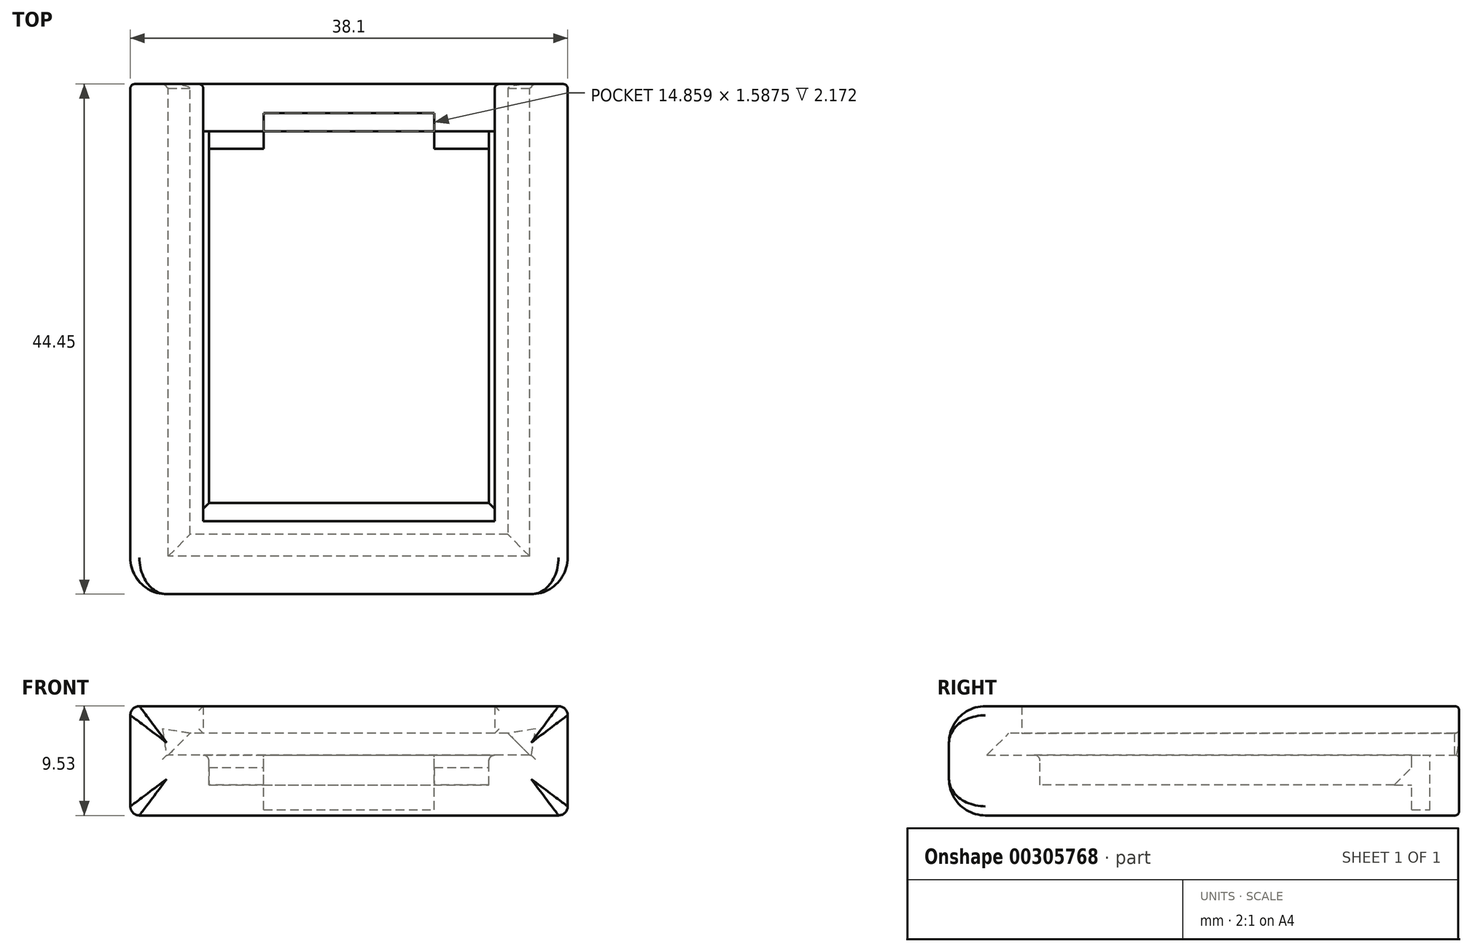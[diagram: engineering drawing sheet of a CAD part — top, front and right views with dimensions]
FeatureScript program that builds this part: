
annotation { "Feature Type Name" : "Feature", "Feature Type Description" : "" }
export const myFeature = defineFeature(function(context is Context, id is Id, definition is map)
    precondition{}
    {
        {
            var Q0;
            Q0=qCreatedBy(makeId("Top.planeOp"),FACE);
            var sketch = newSketch(context, id + "F0", { "sketchPlane" : qUnion([Q0])});
            skLineSegment(sketch, "E0.bottom", {"start": v(0, 0) * mm, "end": v(38.1, 0) * mm});
            skLineSegment(sketch, "E0.top", {"start": v(0, 44.45) * mm, "end": v(38.1, 44.45) * mm});
            skLineSegment(sketch, "E0.left", {"start": v(0, 0) * mm, "end": v(0, 44.45) * mm});
            skLineSegment(sketch, "E0.right", {"start": v(38.1, 0) * mm, "end": v(38.1, 44.45) * mm});
            skSolve(sketch);
        }
        {
            var Q0;
            Q0=makeQuery(id+"F0.imprint","IMPRINT",FACE,{"disambiguationData":[TD([[makeQuery(id+"F0.imprint","IMPRINT",EDGE,{"derivedFrom":sQuery(id+"F0.wireOp",EDGE,"E0.bottom")}),1.0]])]});
            extrude(context, id + "F1", {"entities" : qUnion([Q0]), "depth" : 9.52 * mm});
        }
        {
            var Q0;
            Q0=makeQuery(id+"F1.opExtrude","CAP_FACE",FACE,{"disambiguationData":[OSD([sQuery(id+"F0.wireOp",EDGE,"E0.bottom"),sQuery(id+"F0.wireOp",EDGE,"E0.top"),sQuery(id+"F0.wireOp",EDGE,"E0.left"),sQuery(id+"F0.wireOp",EDGE,"E0.right")])],"isStart":false});
            var sketch = newSketch(context, id + "F2", { "sketchPlane" : qUnion([Q0])});
            skLineSegment(sketch, "E1.bottom", {"start": v(6.86, 40.32) * mm, "end": v(31.24, 40.32) * mm});
            skLineSegment(sketch, "E1.top", {"start": v(6.86, 7.94) * mm, "end": v(31.24, 7.94) * mm});
            skLineSegment(sketch, "E1.left", {"start": v(6.86, 40.32) * mm, "end": v(6.86, 7.94) * mm});
            skLineSegment(sketch, "E1.right", {"start": v(31.24, 40.32) * mm, "end": v(31.24, 7.94) * mm});
            skSolve(sketch);
        }
        {
            var Q0;
            Q0=makeQuery(id+"F2.imprint","IMPRINT",FACE,{"disambiguationData":[TD([[makeQuery(id+"F2.imprint","IMPRINT",EDGE,{"derivedFrom":sQuery(id+"F2.wireOp",EDGE,"E1.bottom")}),-1.0]])]});
            extrude(context, id + "F3", {"entities" : qUnion([Q0]), "operationType" : NewBodyOperationType.REMOVE, "oppositeDirection" : true, "depth" : 6.86 * mm});
        }
        {
            var Q0;
            Q0=makeQuery(id+"F1.opExtrude","SWEPT_FACE",FACE,{"disambiguationData":[OSD([sQuery(id+"F0.wireOp",EDGE,"E0.top")])]});
            var sketch = newSketch(context, id + "F4", { "sketchPlane" : qUnion([Q0])});
            skLineSegment(sketch, "E2.bottom", {"start": v(-34.92, 7.16) * mm, "end": v(-3.17, 7.16) * mm});
            skLineSegment(sketch, "E2.top", {"start": v(-34.92, 5.26) * mm, "end": v(-3.17, 5.26) * mm});
            skLineSegment(sketch, "E2.left", {"start": v(-34.92, 7.16) * mm, "end": v(-34.92, 5.26) * mm});
            skLineSegment(sketch, "E2.right", {"start": v(-3.17, 7.16) * mm, "end": v(-3.17, 5.26) * mm});
            skSolve(sketch);
        }
        {
            var Q0;
            Q0=makeQuery(id+"F4.imprint","IMPRINT",FACE,{"disambiguationData":[TD([[makeQuery(id+"F4.imprint","IMPRINT",EDGE,{"derivedFrom":sQuery(id+"F4.wireOp",EDGE,"E2.bottom")}),-1.0]])]});
            extrude(context, id + "F5", {"entities" : qUnion([Q0]), "operationType" : NewBodyOperationType.REMOVE, "oppositeDirection" : true, "depth" : 41.27 * mm});
        }
        {
            var Q0;
            Q0=makeQuery(id+"F1.opExtrude","SWEPT_FACE",FACE,{"disambiguationData":[OSD([sQuery(id+"F0.wireOp",EDGE,"E0.top")])]});
            var sketch = newSketch(context, id + "F6", { "sketchPlane" : qUnion([Q0])});
            skLineSegment(sketch, "E3.bottom", {"start": v(-31.75, 9.53) * mm, "end": v(-6.35, 9.53) * mm});
            skLineSegment(sketch, "E3.top", {"start": v(-31.75, 7.16) * mm, "end": v(-6.35, 7.16) * mm});
            skLineSegment(sketch, "E3.left", {"start": v(-31.75, 9.53) * mm, "end": v(-31.75, 7.16) * mm});
            skLineSegment(sketch, "E3.right", {"start": v(-6.35, 9.53) * mm, "end": v(-6.35, 7.16) * mm});
            skSolve(sketch);
        }
        {
            var Q0;
            Q0=makeQuery(id+"F6.imprint","IMPRINT",FACE,{"disambiguationData":[TD([[makeQuery(id+"F6.imprint","IMPRINT",EDGE,{"derivedFrom":sQuery(id+"F6.wireOp",EDGE,"E3.bottom")}),1.0]])]});
            extrude(context, id + "F7", {"entities" : qUnion([Q0]), "operationType" : NewBodyOperationType.REMOVE, "oppositeDirection" : true, "depth" : 38.1 * mm});
        }
        {
            var Q0;
            Q0=makeQuery(id+"F5.boolean.opBoolean","COPY",FACE,{"derivedFrom":makeQuery(id+"F5.opExtrude","SWEPT_FACE",FACE,{"disambiguationData":[OSD([sQuery(id+"F4.wireOp",EDGE,"E2.top")])]})});
            var sketch = newSketch(context, id + "F8", { "sketchPlane" : qUnion([Q0])});
            skLineSegment(sketch, "E4.bottom", {"start": v(11.62, 40.32) * mm, "end": v(26.48, 40.32) * mm});
            skLineSegment(sketch, "E4.top", {"start": v(11.62, 41.91) * mm, "end": v(26.48, 41.91) * mm});
            skLineSegment(sketch, "E4.left", {"start": v(11.62, 40.32) * mm, "end": v(11.62, 41.91) * mm});
            skLineSegment(sketch, "E4.right", {"start": v(26.48, 40.32) * mm, "end": v(26.48, 41.91) * mm});
            skSolve(sketch);
        }
        {
            var Q0;
            Q0=makeQuery(id+"F8.imprint","IMPRINT",FACE,{"disambiguationData":[TD([[makeQuery(id+"F8.imprint","IMPRINT",EDGE,{"derivedFrom":sQuery(id+"F8.wireOp",EDGE,"E4.bottom")}),1.0]])]});
            extrude(context, id + "F9", {"entities" : qUnion([Q0]), "operationType" : NewBodyOperationType.REMOVE, "oppositeDirection" : true, "depth" : 4.76 * mm});
        }
        {
            var Q0;
            {var subQ0=sQuery(id+"F2.wireOp",EDGE,"E1.bottom");Q0=makeQuery(id+"F9.boolean.opBoolean","SPLIT",EDGE,{"disambiguationData":[topologyDisambiguationEdgeConnected([makeQuery(id+"F3.boolean.opBoolean","COPY",FACE,{"derivedFrom":makeQuery(id+"F3.opExtrude","CAP_FACE",FACE,{"disambiguationData":[OSD([subQ0,sQuery(id+"F2.wireOp",EDGE,"E1.top"),sQuery(id+"F2.wireOp",EDGE,"E1.left"),sQuery(id+"F2.wireOp",EDGE,"E1.right")])],"isStart":false})}),makeQuery(id+"F9.opExtrude","SWEPT_FACE",FACE,{"disambiguationData":[OSD([sQuery(id+"F8.wireOp",EDGE,"E4.bottom")])]})])],"derivedFrom":makeQuery(id+"F3.boolean.opBoolean","COPY",EDGE,{"derivedFrom":makeQuery(id+"F3.opExtrude","CAP_EDGE",EDGE,{"disambiguationData":[OSD([subQ0])],"isStart":false})})});}
            var Q1;
            Q1=makeQuery(id+"F9.boolean.opBoolean","COPY",EDGE,{"derivedFrom":makeQuery(id+"F9.opExtrude","CAP_EDGE",EDGE,{"disambiguationData":[OSD([sQuery(id+"F8.wireOp",EDGE,"E4.left")])],"isStart":true})});
            var Q2;
            Q2=makeQuery(id+"F9.boolean.opBoolean","COPY",EDGE,{"derivedFrom":makeQuery(id+"F9.opExtrude","CAP_EDGE",EDGE,{"disambiguationData":[OSD([sQuery(id+"F8.wireOp",EDGE,"E4.right")])],"isStart":true})});
            chamfer(context, id + "F10", {"entities" : qUnion([Q0, Q1, Q2]), "width" : 1.52 * mm, "tangentPropagation" : true});
        }
        {
            var Q0;
            Q0=makeQuery(id+"F5.boolean.opBoolean","COPY",FACE,{"derivedFrom":makeQuery(id+"F5.opExtrude","SWEPT_FACE",FACE,{"disambiguationData":[OSD([sQuery(id+"F4.wireOp",EDGE,"E2.bottom")])]})});
            var sketch = newSketch(context, id + "F11", { "sketchPlane" : qUnion([Q0])});
            skLineSegment(sketch, "E5.bottom", {"start": v(15.87, -4.03) * mm, "end": v(19.05, -4.03) * mm});
            skLineSegment(sketch, "E5.top", {"start": v(15.87, -4.81) * mm, "end": v(19.05, -4.81) * mm});
            skLineSegment(sketch, "E5.left", {"start": v(15.87, -4.03) * mm, "end": v(15.87, -4.81) * mm});
            skLineSegment(sketch, "E5.right", {"start": v(19.05, -4.03) * mm, "end": v(19.05, -4.81) * mm});
            skSolve(sketch);
        }
        {
            var Q0;
            Q0=makeQuery(id+"F11.imprint","IMPRINT",FACE,{"disambiguationData":[TD([[makeQuery(id+"F11.imprint","IMPRINT",EDGE,{"derivedFrom":sQuery(id+"F11.wireOp",EDGE,"E5.bottom")}),-1.0]])]});
            extrude(context, id + "F12", {"entities" : qUnion([Q0]), "operationType" : NewBodyOperationType.ADD, "depth" : 0.4 * mm});
        }
        {
            var Q0;
            Q0=makeQuery(id+"F12.opExtrude","CAP_EDGE",EDGE,{"disambiguationData":[OSD([sQuery(id+"F11.wireOp",EDGE,"E5.top")])],"isStart":false});
            var Q1;
            Q1=makeQuery(id+"F12.opExtrude","CAP_EDGE",EDGE,{"disambiguationData":[OSD([sQuery(id+"F11.wireOp",EDGE,"E5.bottom")])],"isStart":false});
            fillet(context, id + "F13", {"entities" : qUnion([Q0, Q1]), "radius" : 0.4 * mm, "tangentPropagation" : true, "allowEdgeOverflow" : false});
        }
        {
            var Q0;
            Q0=makeQuery(id+"F13.opFillet","BLEND_EDGE",EDGE,{"blendedFrom":[makeQuery(id+"F12.opExtrude","CAP_EDGE",EDGE,{"disambiguationData":[OSD([sQuery(id+"F11.wireOp",EDGE,"E5.top")])],"isStart":false}),makeQuery(id+"F12.opExtrude","SWEPT_FACE",FACE,{"disambiguationData":[OSD([sQuery(id+"F11.wireOp",EDGE,"E5.right")])]})],"blendedInto":[makeQuery(id+"F12.opExtrude","SWEPT_FACE",FACE,{"disambiguationData":[OSD([sQuery(id+"F11.wireOp",EDGE,"E5.right")])]})]});
            var Q1;
            Q1=makeQuery(id+"F13.opFillet","BLEND_EDGE",EDGE,{"blendedFrom":[makeQuery(id+"F12.opExtrude","CAP_EDGE",EDGE,{"disambiguationData":[OSD([sQuery(id+"F11.wireOp",EDGE,"E5.bottom")])],"isStart":false}),makeQuery(id+"F12.opExtrude","SWEPT_FACE",FACE,{"disambiguationData":[OSD([sQuery(id+"F11.wireOp",EDGE,"E5.right")])]})],"blendedInto":[makeQuery(id+"F12.opExtrude","SWEPT_FACE",FACE,{"disambiguationData":[OSD([sQuery(id+"F11.wireOp",EDGE,"E5.right")])]})]});
            var Q2;
            Q2=makeQuery(id+"F13.opFillet","BLEND_EDGE",EDGE,{"blendedFrom":[makeQuery(id+"F12.opExtrude","CAP_EDGE",EDGE,{"disambiguationData":[OSD([sQuery(id+"F11.wireOp",EDGE,"E5.top")])],"isStart":false}),makeQuery(id+"F12.opExtrude","SWEPT_FACE",FACE,{"disambiguationData":[OSD([sQuery(id+"F11.wireOp",EDGE,"E5.left")])]})],"blendedInto":[makeQuery(id+"F12.opExtrude","SWEPT_FACE",FACE,{"disambiguationData":[OSD([sQuery(id+"F11.wireOp",EDGE,"E5.left")])]})]});
            var Q3;
            Q3=makeQuery(id+"F13.opFillet","BLEND_EDGE",EDGE,{"blendedFrom":[makeQuery(id+"F12.opExtrude","CAP_EDGE",EDGE,{"disambiguationData":[OSD([sQuery(id+"F11.wireOp",EDGE,"E5.bottom")])],"isStart":false}),makeQuery(id+"F12.opExtrude","SWEPT_FACE",FACE,{"disambiguationData":[OSD([sQuery(id+"F11.wireOp",EDGE,"E5.left")])]})],"blendedInto":[makeQuery(id+"F12.opExtrude","SWEPT_FACE",FACE,{"disambiguationData":[OSD([sQuery(id+"F11.wireOp",EDGE,"E5.left")])]})]});
            fillet(context, id + "F14", {"entities" : qUnion([Q0, Q1, Q2, Q3]), "radius" : 0.38 * mm, "tangentPropagation" : true, "allowEdgeOverflow" : false});
        }
        {
            var Q0;
            Q0=makeQuery(id+"F1.opExtrude","CAP_EDGE",EDGE,{"disambiguationData":[OSD([sQuery(id+"F0.wireOp",EDGE,"E0.left")])],"isStart":false});
            var Q1;
            Q1=makeQuery(id+"F1.opExtrude","CAP_EDGE",EDGE,{"disambiguationData":[OSD([sQuery(id+"F0.wireOp",EDGE,"E0.right")])],"isStart":false});
            var Q2;
            Q2=makeQuery(id+"F1.opExtrude","CAP_EDGE",EDGE,{"disambiguationData":[OSD([sQuery(id+"F0.wireOp",EDGE,"E0.left")])],"isStart":true});
            var Q3;
            Q3=makeQuery(id+"F1.opExtrude","CAP_EDGE",EDGE,{"disambiguationData":[OSD([sQuery(id+"F0.wireOp",EDGE,"E0.right")])],"isStart":true});
            fillet(context, id + "F15", {"entities" : qUnion([Q0, Q1, Q2, Q3]), "radius" : 0.8 * mm, "tangentPropagation" : true, "allowEdgeOverflow" : false});
        }
        {
            var Q0;
            Q0=makeQuery(id+"F1.opExtrude","SWEPT_FACE",FACE,{"disambiguationData":[OSD([sQuery(id+"F0.wireOp",EDGE,"E0.bottom")])]});
            fillet(context, id + "F16", {"entities" : qUnion([Q0]), "radius" : 3.17 * mm, "tangentPropagation" : true, "allowEdgeOverflow" : false});
        }
        {
            var Q0;
            Q0=makeQuery(id+"F1.opExtrude","SWEPT_FACE",FACE,{"disambiguationData":[OSD([sQuery(id+"F0.wireOp",EDGE,"E0.top")])]});
            fillet(context, id + "F17", {"entities" : qUnion([Q0]), "radius" : 0.38 * mm, "tangentPropagation" : true, "allowEdgeOverflow" : false});
        }
        {
            var Q0;
            Q0=makeQuery(id+"F5.boolean.opBoolean","INTERSECT",EDGE,{"derivedFrom":[makeQuery(id+"F3.boolean.opBoolean","COPY",FACE,{"derivedFrom":makeQuery(id+"F3.opExtrude","SWEPT_FACE",FACE,{"disambiguationData":[OSD([sQuery(id+"F2.wireOp",EDGE,"E1.left")])]})}),makeQuery(id+"F5.opExtrude","SWEPT_FACE",FACE,{"disambiguationData":[OSD([sQuery(id+"F4.wireOp",EDGE,"E2.top")])]})]});
            var Q1;
            Q1=makeQuery(id+"F5.boolean.opBoolean","INTERSECT",EDGE,{"derivedFrom":[makeQuery(id+"F3.boolean.opBoolean","COPY",FACE,{"derivedFrom":makeQuery(id+"F3.opExtrude","SWEPT_FACE",FACE,{"disambiguationData":[OSD([sQuery(id+"F2.wireOp",EDGE,"E1.right")])]})}),makeQuery(id+"F5.opExtrude","SWEPT_FACE",FACE,{"disambiguationData":[OSD([sQuery(id+"F4.wireOp",EDGE,"E2.top")])]})]});
            var Q2;
            Q2=makeQuery(id+"F5.boolean.opBoolean","INTERSECT",EDGE,{"derivedFrom":[makeQuery(id+"F3.boolean.opBoolean","COPY",FACE,{"derivedFrom":makeQuery(id+"F3.opExtrude","SWEPT_FACE",FACE,{"disambiguationData":[OSD([sQuery(id+"F2.wireOp",EDGE,"E1.top")])]})}),makeQuery(id+"F5.opExtrude","SWEPT_FACE",FACE,{"disambiguationData":[OSD([sQuery(id+"F4.wireOp",EDGE,"E2.top")])]})]});
            fillet(context, id + "F18", {"entities" : qUnion([Q0, Q1, Q2]), "radius" : 0.5 * mm, "tangentPropagation" : true, "allowEdgeOverflow" : false});
        }
        {
            var Q0;
            Q0=makeQuery(id+"F5.boolean.opBoolean","COPY",EDGE,{"derivedFrom":makeQuery(id+"F5.opExtrude","SWEPT_EDGE",EDGE,{"disambiguationData":[OSD([sQuery(id+"F4.wireOp",EDGE,"E2.bottom"),sQuery(id+"F4.wireOp",EDGE,"E2.left")])]})});
            var Q1;
            Q1=makeQuery(id+"F5.boolean.opBoolean","COPY",EDGE,{"derivedFrom":makeQuery(id+"F5.opExtrude","SWEPT_EDGE",EDGE,{"disambiguationData":[OSD([sQuery(id+"F4.wireOp",EDGE,"E2.bottom"),sQuery(id+"F4.wireOp",EDGE,"E2.right")])]})});
            var Q2;
            Q2=makeQuery(id+"F5.boolean.opBoolean","COPY",EDGE,{"derivedFrom":makeQuery(id+"F5.opExtrude","CAP_EDGE",EDGE,{"disambiguationData":[OSD([sQuery(id+"F4.wireOp",EDGE,"E2.bottom")])],"isStart":false})});
            chamfer(context, id + "F19", {"entities" : qUnion([Q0, Q1, Q2]), "width" : 2.03 * mm, "tangentPropagation" : true});
        }
    });
